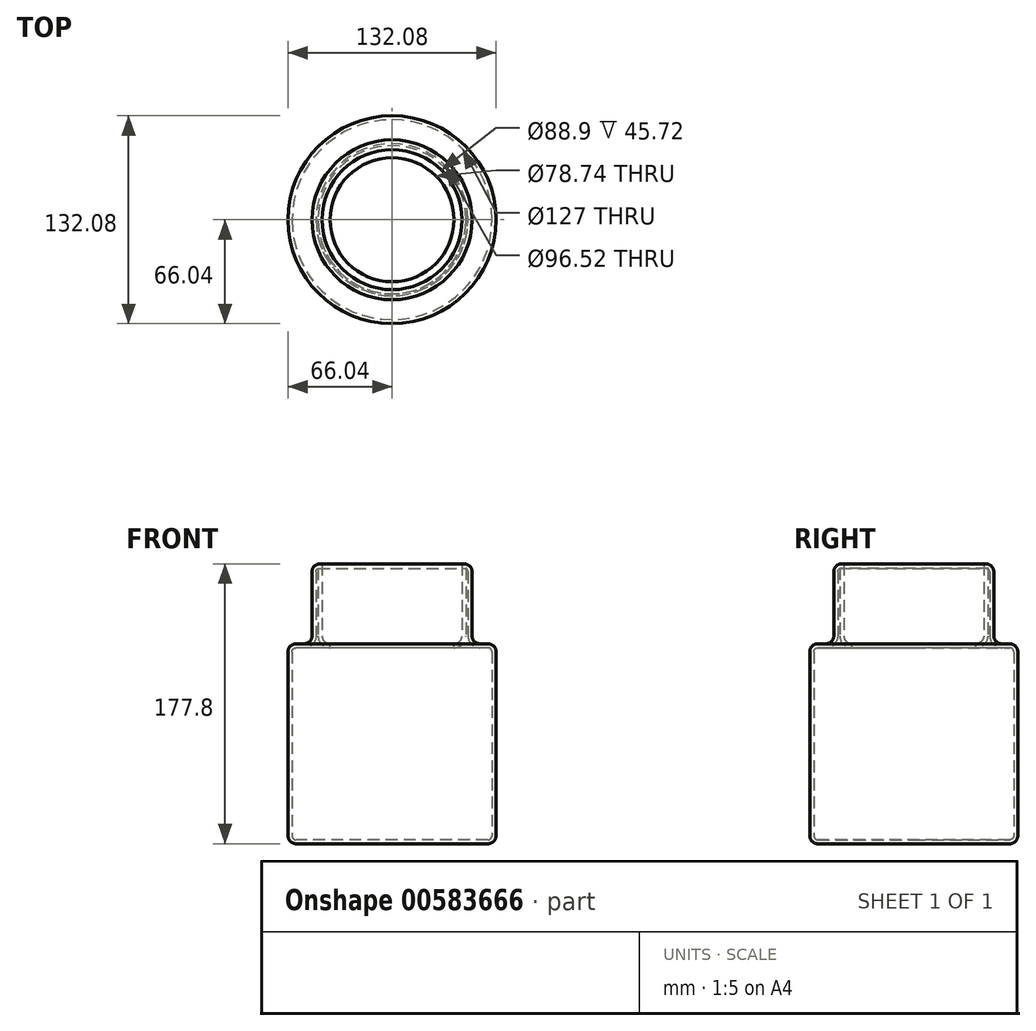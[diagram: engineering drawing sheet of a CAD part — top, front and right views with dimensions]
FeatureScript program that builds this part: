
annotation { "Feature Type Name" : "Feature", "Feature Type Description" : "" }
export const myFeature = defineFeature(function(context is Context, id is Id, definition is map)
    precondition{}
    {
        {
            var Q0;
            Q0=qCreatedBy(makeId("Top.planeOp"),FACE);
            var sketch = newSketch(context, id + "F0", { "sketchPlane" : qUnion([Q0])});
            skCircle(sketch, "E0", {"center": v(0, 0) * mm, "radius": 66.04 * mm});
            skSolve(sketch);
        }
        {
            var Q0;
            Q0 = qSketchRegion(id + "F0", true);
            extrude(context, id + "F1", {"entities" : qUnion([Q0]), "depth" : 127 * mm, "offsetDistance" : 25.4 * mm});
        }
        {
            var Q0;
            Q0=makeQuery(id+"F1.opExtrude","CAP_FACE",FACE,{"disambiguationData":[OSD([sQuery(id+"F0.wireOp",EDGE,"E0")])],"isStart":false});
            var Q1;
            Q1=makeQuery(id+"F1.opExtrude","CAP_FACE",FACE,{"disambiguationData":[OSD([sQuery(id+"F0.wireOp",EDGE,"E0")])],"isStart":true});
            fillet(context, id + "F2", {"entities" : qUnion([Q0, Q1]), "radius" : 5.08 * mm, "tangentPropagation" : true, "allowEdgeOverflow" : false});
        }
        {
            var Q0;
            Q0=makeQuery(id+"F1.opExtrude","CAP_FACE",FACE,{"disambiguationData":[OSD([sQuery(id+"F0.wireOp",EDGE,"E0")])],"isStart":false});
            var sketch = newSketch(context, id + "F3", { "sketchPlane" : qUnion([Q0])});
            skCircle(sketch, "E1", {"center": v(0, 0) * mm, "radius": 50.8 * mm});
            skCircle(sketch, "E2", {"center": v(0, 0) * mm, "radius": 44.45 * mm});
            skSolve(sketch);
        }
        {
            var Q0;
            Q0 = qSketchRegion(id + "F3", true);
            extrude(context, id + "F4", {"entities" : qUnion([Q0]), "operationType" : NewBodyOperationType.ADD, "depth" : 50.8 * mm, "offsetDistance" : 25.4 * mm});
        }
        {
            var Q0;
            Q0=makeQuery(id+"F4.opExtrude","SWEPT_FACE",FACE,{"disambiguationData":[OSD([sQuery(id+"F3.wireOp",EDGE,"E1")])]});
            var Q1;
            Q1=makeQuery(id+"F4.boolean.opBoolean","SPLIT",FACE,{"disambiguationData":[TD([makeQuery(id+"F4.opExtrude","SWEPT_FACE",FACE,{"disambiguationData":[OSD([sQuery(id+"F3.wireOp",EDGE,"E2")])]})])],"derivedFrom":makeQuery(id+"F1.opExtrude","CAP_FACE",FACE,{"disambiguationData":[OSD([sQuery(id+"F0.wireOp",EDGE,"E0")])],"isStart":false})});
            fillet(context, id + "F5", {"entities" : qUnion([Q0, Q1]), "radius" : 5.08 * mm, "tangentPropagation" : true, "allowEdgeOverflow" : false});
        }
        {
            var Q0;
            Q0=makeQuery(id+"F4.boolean.opBoolean","SPLIT",FACE,{"disambiguationData":[TD([makeQuery(id+"F4.opExtrude","SWEPT_FACE",FACE,{"disambiguationData":[OSD([sQuery(id+"F3.wireOp",EDGE,"E2")])]})])],"derivedFrom":makeQuery(id+"F1.opExtrude","CAP_FACE",FACE,{"disambiguationData":[OSD([sQuery(id+"F0.wireOp",EDGE,"E0")])],"isStart":false})});
            shell(context, id + "F6", {"entities" : qUnion([Q0]), "thickness" : 2.54 * mm});
        }
    });
